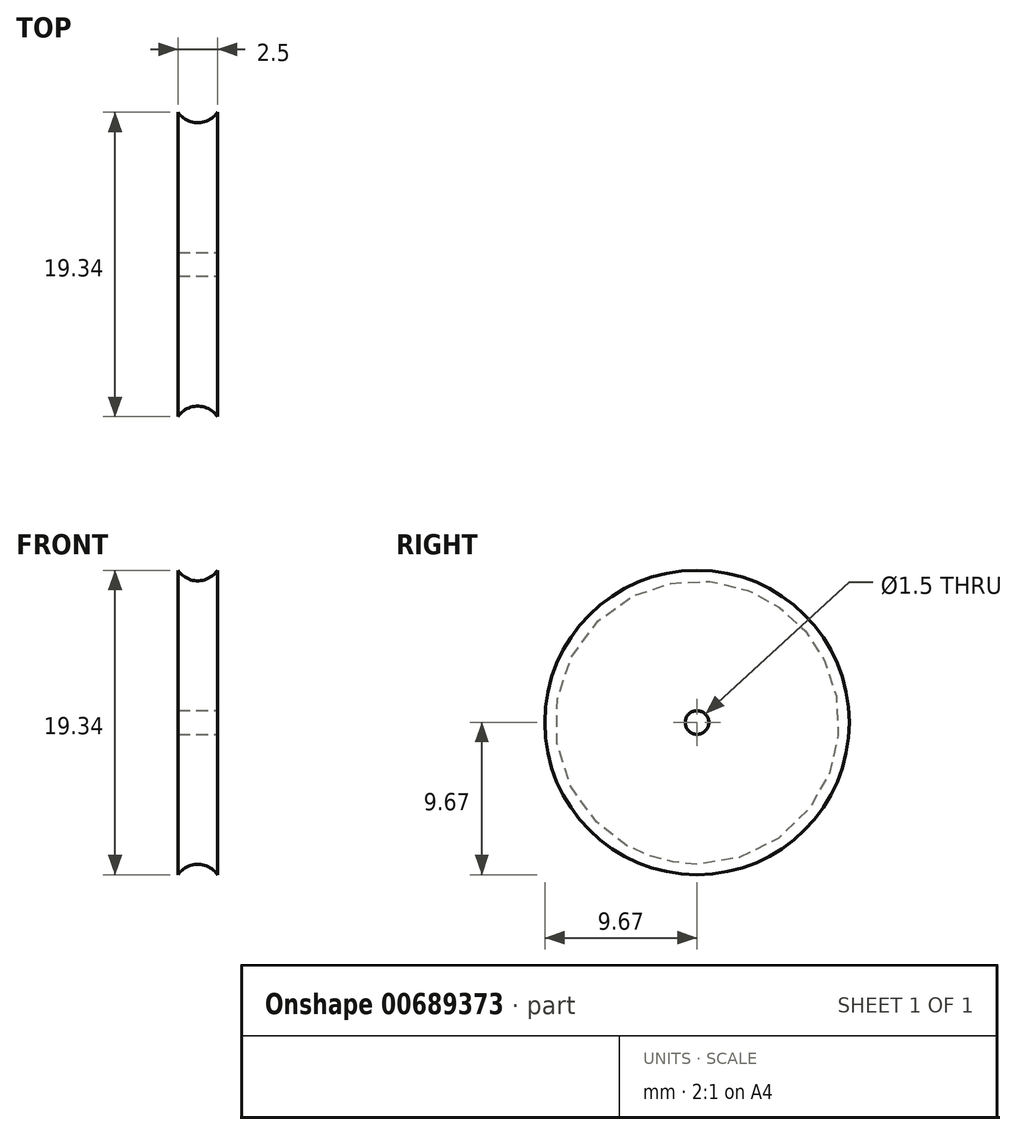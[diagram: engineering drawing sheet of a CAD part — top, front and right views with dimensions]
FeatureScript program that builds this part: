
annotation { "Feature Type Name" : "Feature", "Feature Type Description" : "" }
export const myFeature = defineFeature(function(context is Context, id is Id, definition is map)
    precondition{}
    {
        {
            var Q0;
            Q0=qCreatedBy(makeId("Front.planeOp"),FACE);
            var sketch = newSketch(context, id + "F0", { "sketchPlane" : qUnion([Q0])});
            skArc(sketch, "E0", {"start": v(-1.25, 9.67) * mm, "mid": v(0, 9) * mm, "end": v(1.25, 9.67) * mm});
            skLineSegment(sketch, "E1", {"start": v(-1.25, 0.75) * mm, "end": v(-1.25, 9.67) * mm});
            skLineSegment(sketch, "E2", {"start": v(1.25, 0.75) * mm, "end": v(1.25, 9.67) * mm});
            skLineSegment(sketch, "E3", {"start": v(1.25, 0.75) * mm, "end": v(-1.25, 0.75) * mm});
            skPoint(sketch, "E4.orphan", {"position": v(1.25, 0) * mm});
            skPoint(sketch, "E5.orphan", {"position": v(-1.25, 0) * mm});
            skSolve(sketch);
        }
        {
            var Q0;
            Q0=qCreatedBy(makeId("Top.planeOp"),FACE);
            var sketch = newSketch(context, id + "F1", { "sketchPlane" : qUnion([Q0])});
            skLineSegment(sketch, "E6", {"start": v(15.52, 0) * mm, "end": v(-20.2, 0) * mm});
            skSolve(sketch);
        }
        {
            var Q0;
            Q0=qSketchRegion(id+"F0",true);
            var Q1;
            Q1=sQuery(id+"F1.wireOp",EDGE,"E6");
            revolve(context, id + "F2", {"entities" : qUnion([Q0]), "axis" : qUnion([Q1]), "revolveType" : RevolveType.FULL});
        }
    });
